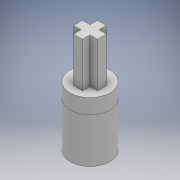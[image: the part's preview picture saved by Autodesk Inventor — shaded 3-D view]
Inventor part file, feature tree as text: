
AUTODESK INVENTOR PART (.ipt)
format: ipt  version: 2018.2 (Build 222227000, 227)  size: 133,632 bytes
history: native  units: mm
features: extrude x4, sketch x4
ambient origin geometry x8: Origin, YZ Plane, XZ Plane, XY Plane, X Axis, Y Axis, Z Axis, Center Point
bodies: Solid1 (feature_tree)
feature tree (8):
  extrude  "Extrusion1"  Depth=8.0mm
  extrude  "Extrusion2"  Depth=3.0mm TaperAngle=0.0deg
  extrude  "Extrusion3"  Depth=1.8mm
  extrude  "Extrusion4"  Depth=1.8mm
  sketch  "Sketch1"  dims[d0=4.25mm d1=8.0mm]
  sketch  "Sketch2"  dims[d2=9.0mm d3=0.0mm d4=3.0mm d5=0.0mm]
  sketch  "Sketch3"  dims[d6=4.8mm d7=1.8mm]
  sketch  "Sketch4"  dims[d8=2.4mm d10=1.8mm d11=4.8mm d12=2.4mm d14=9.0mm d15=0.0mm d19=9.0mm d20=0.0mm]
